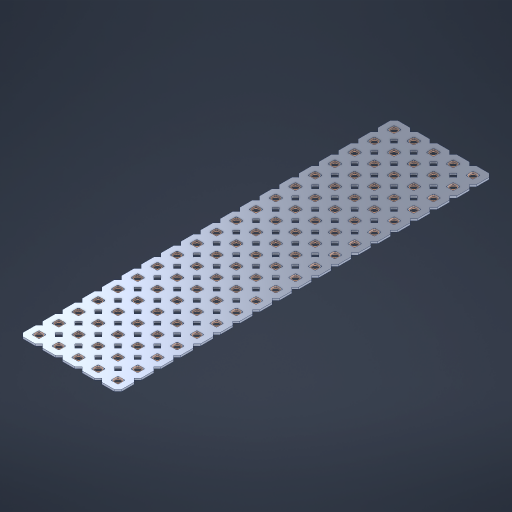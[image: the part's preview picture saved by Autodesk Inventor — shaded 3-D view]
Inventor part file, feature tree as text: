
AUTODESK INVENTOR PART (.ipt)
format: ipt  version: 2023 (Build 270158000, 158)  size: 1,358,848 bytes
history: native  units: in
note: dims shown in document units (in); Inventor stores cm internally (conversion verified against a paired STEP export)
features: other x96, extrude x94, sketch x2, pattern_linear x1
ambient origin geometry x8: Origin, YZ Plane, XZ Plane, XY Plane, X Axis, Y Axis, Z Axis, Center Point
bodies: Solid1 (feature_tree), Body (feature_tree)
feature tree (193):
  pattern_linear  "Rectangular Pattern1"  Spacing1=0.09in  [1 undecoded]
  sketch  "Sketch1"  dims[d1=0.5in]
  sketch  "Sketch2"  dims[d2=0.182in d3=0.09in d4=0.09in d5=0.09in d6=0.09in d7=0.09in d8=0.09in d9=0.09in d10=0.09in d11=0.02in d13=0.0in d14=0.172in d15=0.0625in d16=0.0in d19=0.5in d22=0.5in]
  other  "Srf1"
  other  "Srf126"
  other  "Srf127"
  other  "Srf128"
  other  "Srf129"
  other  "Srf130"
  other  "Srf131"
  other  "Srf250"
  other  "Srf251"
  other  "Srf252"
  other  "Srf253"
  other  "Srf254"
  other  "Srf255"
  other  "Srf256"
  other  "Srf257"
  other  "Srf258"
  other  "Srf259"
  other  "Srf260"
  other  "Srf261"
  other  "Srf268"
  other  "Srf269"
  other  "Srf270"
  other  "Srf271"
  other  "Srf272"
  other  "Srf273"
  other  "Srf274"
  other  "Srf275"
  other  "Srf276"
  other  "Srf277"
  other  "Srf278"
  other  "Srf279"
  other  "Srf280"
  other  "Srf281"
  other  "Srf282"
  other  "Srf283"
  other  "Srf284"
  other  "Srf285"
  other  "Srf286"
  other  "Srf293"
  other  "Srf294"
  other  "Srf295"
  other  "Srf296"
  other  "Srf297"
  other  "Srf298"
  other  "Srf299"
  other  "Srf300"
  other  "Srf301"
  other  "Srf302"
  other  "Srf303"
  other  "Srf304"
  other  "Srf305"
  other  "Srf306"
  other  "Srf307"
  other  "Srf308"
  other  "Srf309"
  other  "Srf310"
  other  "Srf311"
  other  "Srf318"
  other  "Srf319"
  other  "Srf320"
  other  "Srf321"
  other  "Srf322"
  other  "Srf323"
  other  "Srf324"
  other  "Srf325"
  other  "Srf326"
  other  "Srf327"
  other  "Srf328"
  other  "Srf329"
  other  "Srf330"
  other  "Srf331"
  other  "Srf332"
  other  "Srf333"
  other  "Srf334"
  other  "Srf335"
  other  "Srf336"
  other  "Srf343"
  other  "Srf344"
  other  "Srf345"
  other  "Srf346"
  other  "Srf347"
  other  "Srf348"
  other  "Srf349"
  other  "Srf350"
  other  "Srf351"
  other  "Srf352"
  other  "Srf353"
  other  "Srf354"
  other  "Srf355"
  other  "Srf356"
  other  "Srf357"
  other  "Srf358"
  other  "Srf359"
  other  "Srf360"
  other  "Srf361"
  other  "Circle"
  extrude  "ExtrusionSrf126"  Depth=0.09in
  extrude  "ExtrusionSrf127"  Depth=0.09in
  extrude  "ExtrusionSrf128"  Depth=0.09in
  extrude  "ExtrusionSrf129"  Depth=0.09in
  extrude  "ExtrusionSrf130"  Depth=0.09in
  extrude  "ExtrusionSrf131"  Depth=0.09in
  extrude  "ExtrusionSrf250"  Depth=0.09in
  extrude  "ExtrusionSrf251"  Depth=0.02in
  extrude  "ExtrusionSrf252"  TaperAngle=0.0deg  [1 undecoded]
  extrude  "ExtrusionSrf253"  Depth=0.5in
  extrude  "ExtrusionSrf254"  Depth=0.5in TaperAngle=0.0deg
  extrude  "ExtrusionSrf255"  Depth=0.5in
  extrude  "ExtrusionSrf256"  Depth=0.5in
  extrude  "ExtrusionSrf257"  [1 undecoded]
  extrude  "ExtrusionSrf258"  [1 undecoded]
  extrude  "ExtrusionSrf259"  [1 undecoded]
  extrude  "ExtrusionSrf260"  [1 undecoded]
  extrude  "ExtrusionSrf261"  [1 undecoded]
  extrude  "ExtrusionSrf268"  [1 undecoded]
  extrude  "ExtrusionSrf269"  [1 undecoded]
  extrude  "ExtrusionSrf270"  [1 undecoded]
  extrude  "ExtrusionSrf271"  [1 undecoded]
  extrude  "ExtrusionSrf272"  [1 undecoded]
  extrude  "ExtrusionSrf273"  [1 undecoded]
  extrude  "ExtrusionSrf274"  [1 undecoded]
  extrude  "ExtrusionSrf275"  [1 undecoded]
  extrude  "ExtrusionSrf276"  [1 undecoded]
  extrude  "ExtrusionSrf277"  [1 undecoded]
  extrude  "ExtrusionSrf278"  [1 undecoded]
  extrude  "ExtrusionSrf279"  [1 undecoded]
  extrude  "ExtrusionSrf280"  [1 undecoded]
  extrude  "ExtrusionSrf281"  [1 undecoded]
  extrude  "ExtrusionSrf282"  [1 undecoded]
  extrude  "ExtrusionSrf283"  [1 undecoded]
  extrude  "ExtrusionSrf284"  [1 undecoded]
  extrude  "ExtrusionSrf285"  [1 undecoded]
  extrude  "ExtrusionSrf286"  [1 undecoded]
  extrude  "ExtrusionSrf293"  [1 undecoded]
  extrude  "ExtrusionSrf294"  [1 undecoded]
  extrude  "ExtrusionSrf295"  [1 undecoded]
  extrude  "ExtrusionSrf296"  [1 undecoded]
  extrude  "ExtrusionSrf297"  [1 undecoded]
  extrude  "ExtrusionSrf298"  [1 undecoded]
  extrude  "ExtrusionSrf299"  [1 undecoded]
  extrude  "ExtrusionSrf300"  [1 undecoded]
  extrude  "ExtrusionSrf301"  [1 undecoded]
  extrude  "ExtrusionSrf302"  [1 undecoded]
  extrude  "ExtrusionSrf303"  [1 undecoded]
  extrude  "ExtrusionSrf304"  [1 undecoded]
  extrude  "ExtrusionSrf305"  [1 undecoded]
  extrude  "ExtrusionSrf306"  [1 undecoded]
  extrude  "ExtrusionSrf307"  [1 undecoded]
  extrude  "ExtrusionSrf308"  [1 undecoded]
  extrude  "ExtrusionSrf309"  [1 undecoded]
  extrude  "ExtrusionSrf310"  [1 undecoded]
  extrude  "ExtrusionSrf311"  [1 undecoded]
  extrude  "ExtrusionSrf318"  [1 undecoded]
  extrude  "ExtrusionSrf319"  [1 undecoded]
  extrude  "ExtrusionSrf320"  [1 undecoded]
  extrude  "ExtrusionSrf321"  [1 undecoded]
  extrude  "ExtrusionSrf322"  [1 undecoded]
  extrude  "ExtrusionSrf323"  [1 undecoded]
  extrude  "ExtrusionSrf324"  [1 undecoded]
  extrude  "ExtrusionSrf325"  [1 undecoded]
  extrude  "ExtrusionSrf326"  [1 undecoded]
  extrude  "ExtrusionSrf327"  [1 undecoded]
  extrude  "ExtrusionSrf328"  [1 undecoded]
  extrude  "ExtrusionSrf329"  [1 undecoded]
  extrude  "ExtrusionSrf330"  [1 undecoded]
  extrude  "ExtrusionSrf331"  [1 undecoded]
  extrude  "ExtrusionSrf332"  [1 undecoded]
  extrude  "ExtrusionSrf333"  [1 undecoded]
  extrude  "ExtrusionSrf334"  [1 undecoded]
  extrude  "ExtrusionSrf335"  [1 undecoded]
  extrude  "ExtrusionSrf336"  [1 undecoded]
  extrude  "ExtrusionSrf343"  [1 undecoded]
  extrude  "ExtrusionSrf344"  [1 undecoded]
  extrude  "ExtrusionSrf345"  [1 undecoded]
  extrude  "ExtrusionSrf346"  [1 undecoded]
  extrude  "ExtrusionSrf347"  [1 undecoded]
  extrude  "ExtrusionSrf348"  [1 undecoded]
  extrude  "ExtrusionSrf349"  [1 undecoded]
  extrude  "ExtrusionSrf350"  [1 undecoded]
  extrude  "ExtrusionSrf351"  [1 undecoded]
  extrude  "ExtrusionSrf352"  [1 undecoded]
  extrude  "ExtrusionSrf353"  [1 undecoded]
  extrude  "ExtrusionSrf354"  [1 undecoded]
  extrude  "ExtrusionSrf355"  [1 undecoded]
  extrude  "ExtrusionSrf356"  [1 undecoded]
  extrude  "ExtrusionSrf357"  [1 undecoded]
  extrude  "ExtrusionSrf358"  [1 undecoded]
  extrude  "ExtrusionSrf359"  [1 undecoded]
  extrude  "ExtrusionSrf360"  [1 undecoded]
  extrude  "ExtrusionSrf361"  [1 undecoded]
note: 83 required parameter values undecoded (feature->parameter linkage not recoverable at this tier; creation-order binding heuristic only, values carry confidence <= 0.55)
